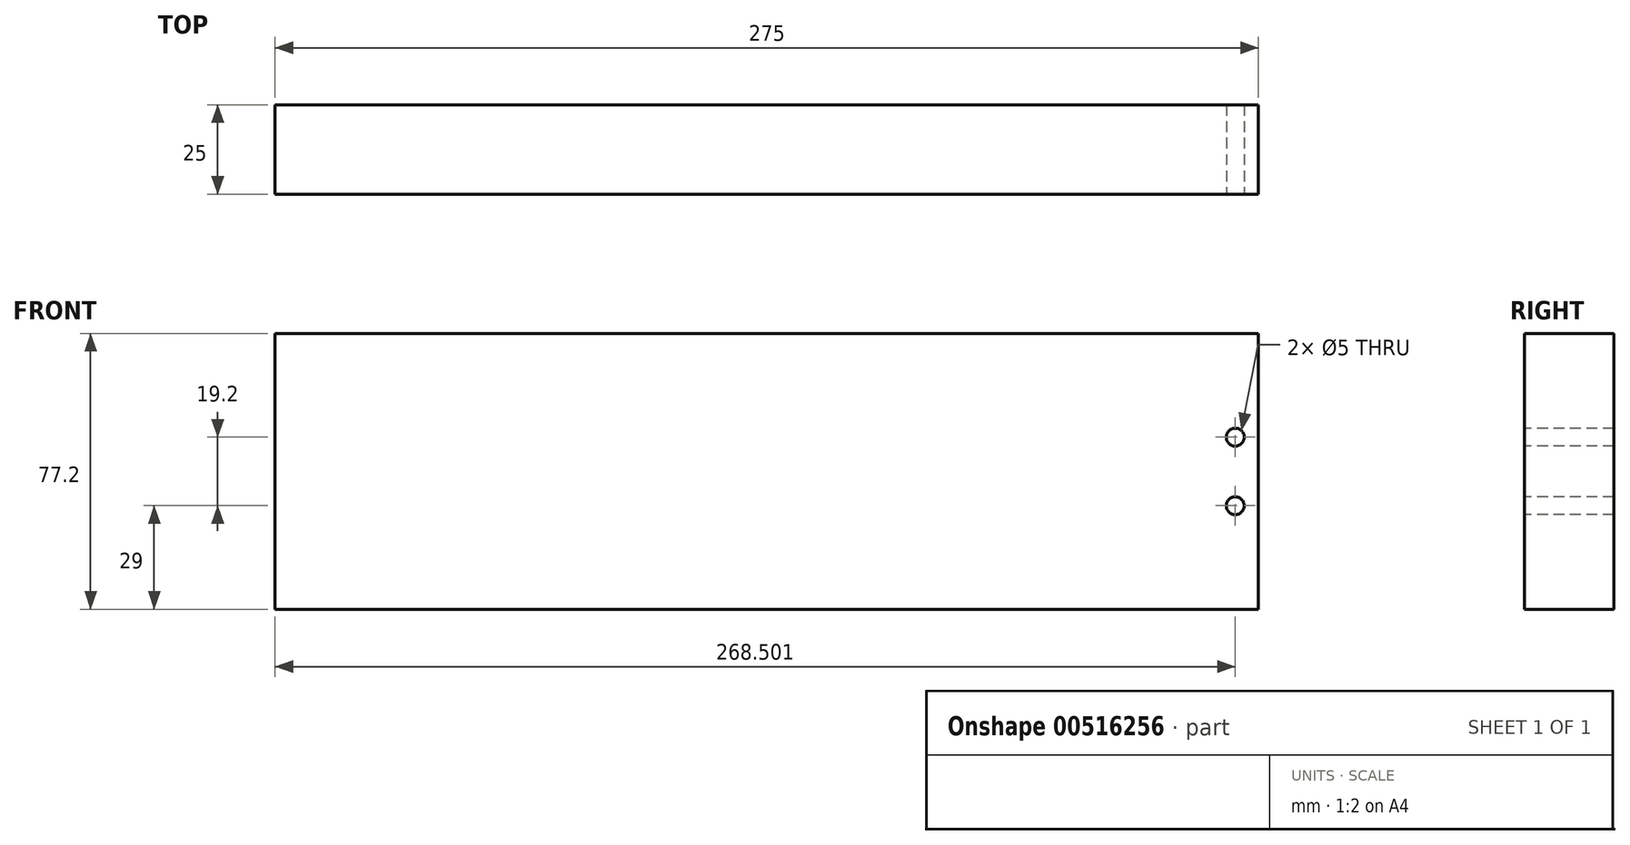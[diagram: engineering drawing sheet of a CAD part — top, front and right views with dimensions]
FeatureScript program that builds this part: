
annotation { "Feature Type Name" : "Feature", "Feature Type Description" : "" }
export const myFeature = defineFeature(function(context is Context, id is Id, definition is map)
    precondition{}
    {
        {
            var Q0;
            Q0=qCreatedBy(makeId("Front.planeOp"),FACE);
            var sketch = newSketch(context, id + "F0", { "sketchPlane" : qUnion([Q0])});
            skLineSegment(sketch, "E0.bottom", {"start": v(145.45, -38.6) * mm, "end": v(-129.55, -38.6) * mm});
            skLineSegment(sketch, "E0.top", {"start": v(145.45, 38.6) * mm, "end": v(-129.55, 38.6) * mm});
            skLineSegment(sketch, "E0.left", {"start": v(145.45, -38.6) * mm, "end": v(145.45, 38.6) * mm});
            skLineSegment(sketch, "E0.right", {"start": v(-129.55, -38.6) * mm, "end": v(-129.55, 38.6) * mm});
            skPoint(sketch, "E0.middle", {"position": v(7.95, 0) * mm});
            skSolve(sketch);
        }
        {
            var Q0;
            Q0 = qSketchRegion(id + "F0", true);
            extrude(context, id + "F1", {"entities" : qUnion([Q0]), "depth" : 25 * mm, "offsetDistance" : 25 * mm});
        }
        {
            var Q0;
            Q0=makeQuery(id+"F1.opExtrude","CAP_FACE",FACE,{"disambiguationData":[OSD([sQuery(id+"F0.wireOp",EDGE,"E0.bottom"),sQuery(id+"F0.wireOp",EDGE,"E0.top"),sQuery(id+"F0.wireOp",EDGE,"E0.left"),sQuery(id+"F0.wireOp",EDGE,"E0.right")])],"isStart":false});
            var sketch = newSketch(context, id + "F2", { "sketchPlane" : qUnion([Q0])});
            skCircle(sketch, "E1", {"center": v(138.95, 9.6) * mm, "radius": 2.5 * mm});
            skCircle(sketch, "E2", {"center": v(138.95, -9.6) * mm, "radius": 2.5 * mm});
            skSolve(sketch);
        }
        {
            var Q0;
            Q0 = qSketchRegion(id + "F2", true);
            extrude(context, id + "F3", {"entities" : qUnion([Q0]), "operationType" : NewBodyOperationType.REMOVE, "oppositeDirection" : true, "depth" : 34.8 * mm, "offsetDistance" : 25 * mm});
        }
    });
